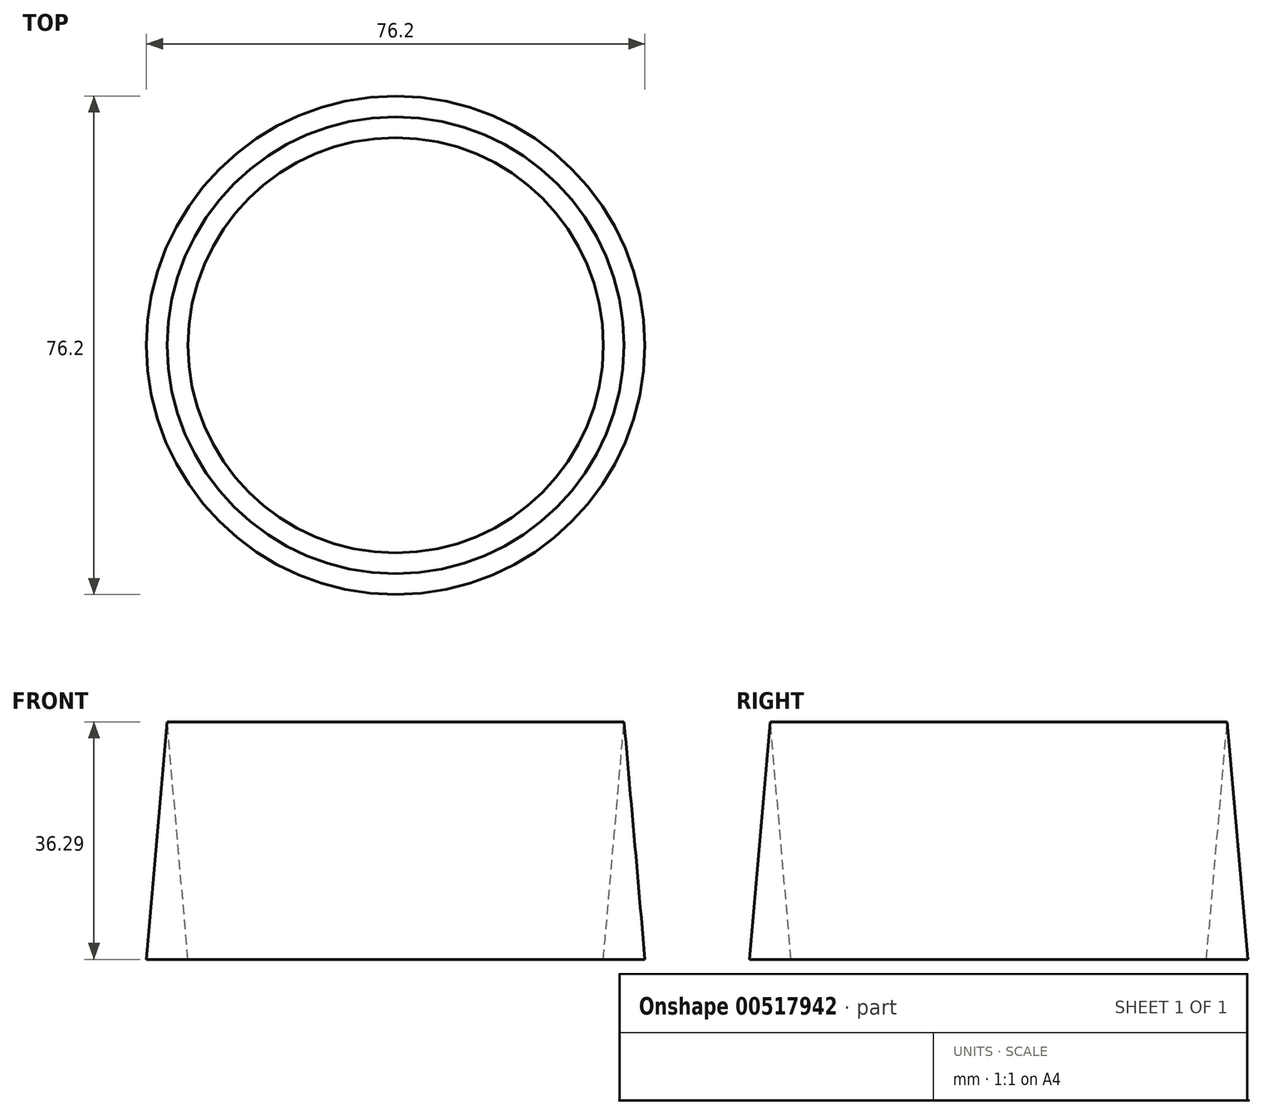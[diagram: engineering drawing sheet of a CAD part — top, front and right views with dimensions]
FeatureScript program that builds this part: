
annotation { "Feature Type Name" : "Feature", "Feature Type Description" : "" }
export const myFeature = defineFeature(function(context is Context, id is Id, definition is map)
    precondition{}
    {
        {
            var Q0;
            Q0=qCreatedBy(makeId("Top.planeOp"),FACE);
            var sketch = newSketch(context, id + "F0", { "sketchPlane" : qUnion([Q0])});
            skCircle(sketch, "E0", {"center": v(0, 0) * mm, "radius": 38.1 * mm});
            skCircle(sketch, "E1", {"center": v(0, 0) * mm, "radius": 31.75 * mm});
            skSolve(sketch);
        }
        {
            var Q0;
            Q0=makeQuery(id+"F0.imprint","IMPRINT",FACE,{"disambiguationData":[TD([[makeQuery(id+"F0.imprint","IMPRINT",EDGE,{"derivedFrom":sQuery(id+"F0.wireOp",EDGE,"E0")}),1.0]])]});
            var Q1;
            Q1=sQuery(id+"F0.wireOp",EDGE,"E0");
            extrude(context, id + "F1", {"entities" : qUnion([Q0]), "surfaceEntities" : qUnion([Q1]), "depth" : 88.9 * mm, "offsetDistance" : 25.4 * mm, "hasDraft" : true, "draftAngle" : 5 * degree, "draftPullDirection" : true});
        }
    });
